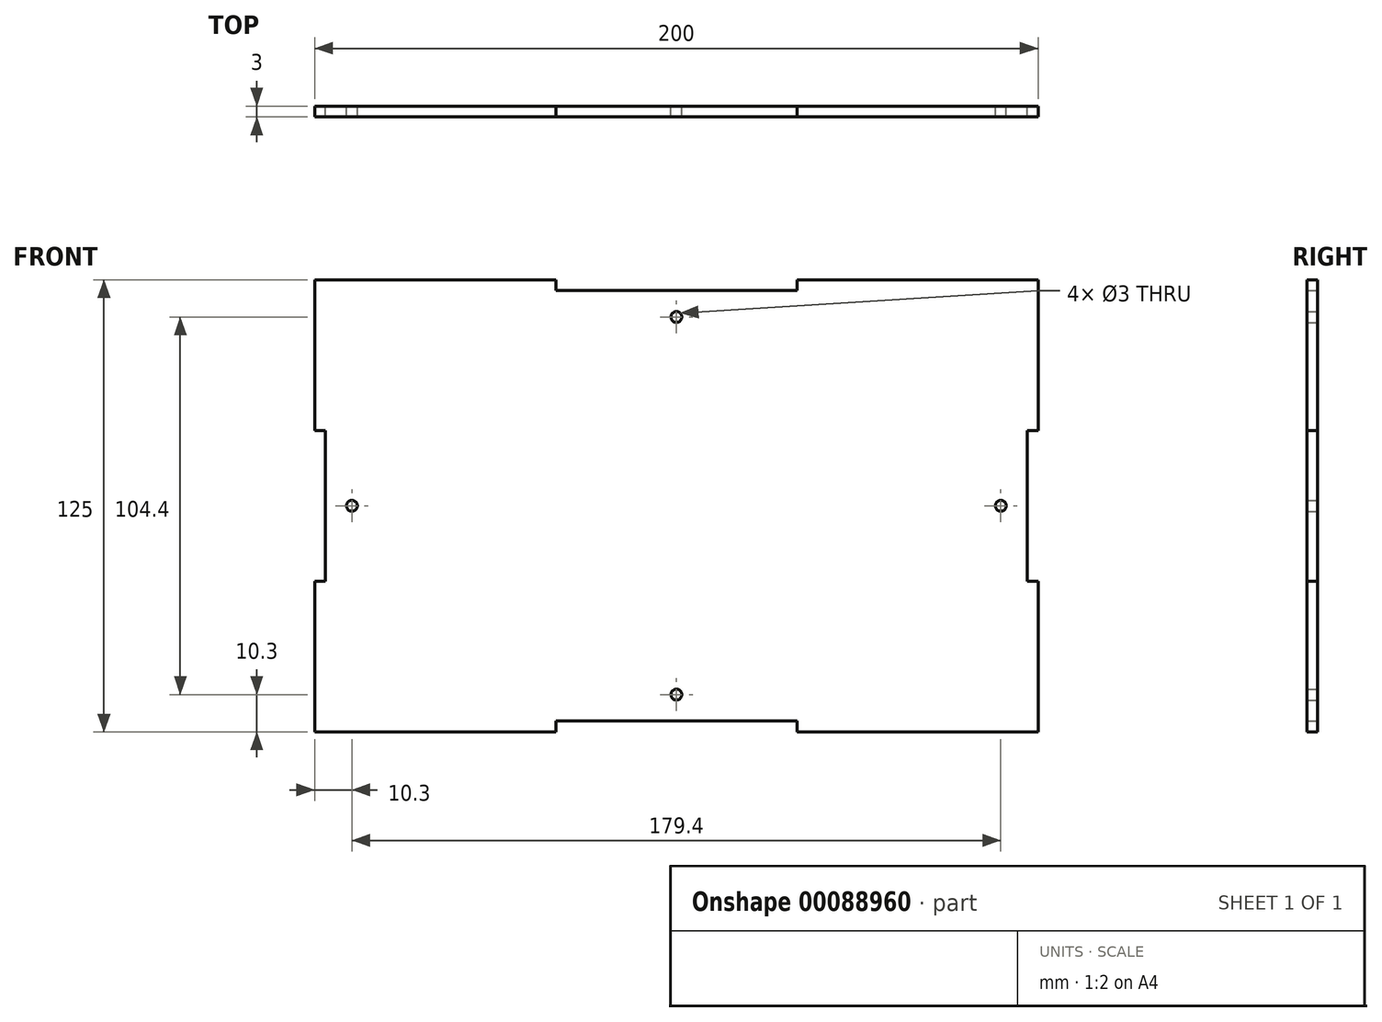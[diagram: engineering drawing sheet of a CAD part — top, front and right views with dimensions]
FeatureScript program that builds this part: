
annotation { "Feature Type Name" : "Feature", "Feature Type Description" : "" }
export const myFeature = defineFeature(function(context is Context, id is Id, definition is map)
    precondition{}
    {
        {
            var Q0;
            Q0=qCreatedBy(makeId("Front.planeOp"),FACE);
            var sketch = newSketch(context, id + "F0", { "sketchPlane" : qUnion([Q0])});
            skLineSegment(sketch, "E0.top", {"start": v(-100, -62.5) * mm, "end": v(-33.33, -62.5) * mm});
            skLineSegment(sketch, "E0.left", {"start": v(-100, 62.5) * mm, "end": v(-100, 20.83) * mm});
            skLineSegment(sketch, "E0.right", {"start": v(100, 62.5) * mm, "end": v(100, 20.83) * mm});
            skLineSegment(sketch, "E1", {"start": v(-100, 62.5) * mm, "end": v(-33.33, 62.5) * mm});
            skLineSegment(sketch, "E2", {"start": v(-33.33, 62.5) * mm, "end": v(-33.33, 59.5) * mm});
            skLineSegment(sketch, "E3", {"start": v(-33.33, 59.5) * mm, "end": v(33.33, 59.5) * mm});
            skLineSegment(sketch, "E4", {"start": v(33.33, 59.5) * mm, "end": v(33.33, 62.5) * mm});
            skLineSegment(sketch, "E5", {"start": v(33.33, 62.5) * mm, "end": v(100, 62.5) * mm});
            skLineSegment(sketch, "E6", {"start": v(100, 20.83) * mm, "end": v(97, 20.83) * mm});
            skLineSegment(sketch, "E7", {"start": v(97, 20.83) * mm, "end": v(97, -20.83) * mm});
            skLineSegment(sketch, "E8", {"start": v(97, -20.83) * mm, "end": v(100, -20.83) * mm});
            skLineSegment(sketch, "E9.trimOffspring", {"start": v(100, -20.83) * mm, "end": v(100, -62.5) * mm});
            skLineSegment(sketch, "E10", {"start": v(-100, 20.83) * mm, "end": v(-97, 20.83) * mm});
            skLineSegment(sketch, "E11", {"start": v(-97, 20.83) * mm, "end": v(-97, -20.83) * mm});
            skLineSegment(sketch, "E12", {"start": v(-97, -20.83) * mm, "end": v(-100, -20.83) * mm});
            skLineSegment(sketch, "E13", {"start": v(-33.33, -62.5) * mm, "end": v(-33.33, -59.5) * mm});
            skLineSegment(sketch, "E14", {"start": v(-33.33, -59.5) * mm, "end": v(33.33, -59.5) * mm});
            skLineSegment(sketch, "E15", {"start": v(33.33, -59.5) * mm, "end": v(33.33, -62.5) * mm});
            skLineSegment(sketch, "E16.trimOffspring", {"start": v(-100, -20.83) * mm, "end": v(-100, -62.5) * mm});
            skLineSegment(sketch, "E17.trimOffspring", {"start": v(33.33, -62.5) * mm, "end": v(100, -62.5) * mm});
            skCircle(sketch, "E18", {"center": v(0, 52.2) * mm, "radius": 1.5 * mm});
            skCircle(sketch, "E19", {"center": v(89.7, 0) * mm, "radius": 1.5 * mm});
            skCircle(sketch, "E20", {"center": v(0, -52.2) * mm, "radius": 1.5 * mm});
            skCircle(sketch, "E21", {"center": v(-89.7, 0) * mm, "radius": 1.5 * mm});
            skSolve(sketch);
        }
        {
            var Q0;
            Q0=qSketchRegion(id+"F0",true);
            extrude(context, id + "F1", {"entities" : qUnion([Q0]), "depth" : 3 * mm});
        }
        {
            var Q0;
            Q0=makeQuery(id+"F1.opExtrude","SWEPT_BODY",BODY,{"disambiguationData":[OSD([sQuery(id+"F0.wireOp",EDGE,"E0.top"),sQuery(id+"F0.wireOp",EDGE,"E0.left"),sQuery(id+"F0.wireOp",EDGE,"E0.right"),sQuery(id+"F0.wireOp",EDGE,"E1"),sQuery(id+"F0.wireOp",EDGE,"E2"),sQuery(id+"F0.wireOp",EDGE,"E3"),sQuery(id+"F0.wireOp",EDGE,"E4"),sQuery(id+"F0.wireOp",EDGE,"E5"),sQuery(id+"F0.wireOp",EDGE,"E6"),sQuery(id+"F0.wireOp",EDGE,"E7"),sQuery(id+"F0.wireOp",EDGE,"E8"),sQuery(id+"F0.wireOp",EDGE,"E9.trimOffspring"),sQuery(id+"F0.wireOp",EDGE,"E10"),sQuery(id+"F0.wireOp",EDGE,"E11"),sQuery(id+"F0.wireOp",EDGE,"E12"),sQuery(id+"F0.wireOp",EDGE,"E13"),sQuery(id+"F0.wireOp",EDGE,"E14"),sQuery(id+"F0.wireOp",EDGE,"E15"),sQuery(id+"F0.wireOp",EDGE,"E16.trimOffspring"),sQuery(id+"F0.wireOp",EDGE,"E17.trimOffspring"),sQuery(id+"F0.wireOp",EDGE,"iJvMOkkT-Gsvz-D80s-Lrck-NuYzV2775GFc"),sQuery(id+"F0.wireOp",EDGE,"95r7G61u-81NE-ogXZ-HZlh-HaEjHri7Uc5C"),sQuery(id+"F0.wireOp",EDGE,"kNa5tEdO-uy4Q-kRTS-gWff-R1CwjTJMmlwP"),sQuery(id+"F0.wireOp",EDGE,"NSmLs8Xq-7i2g-OZIT-hmmc-yelxhuIJ4KvX"),sQuery(id+"F0.wireOp",EDGE,"4YweHJoU-akzP-T6YO-Ozvt-s9SiKn9Ip7Ij"),sQuery(id+"F0.wireOp",EDGE,"DRZYSCKz-exI7-oD3f-2VZ2-mNw9MquuhidN"),sQuery(id+"F0.wireOp",EDGE,"cFZweqHX-i8zY-QQJQ-dr00-DEtuZUepJHJH"),sQuery(id+"F0.wireOp",EDGE,"vflKgIvX-I86b-ziDt-TOTA-sqA9vDxPemz3"),sQuery(id+"F0.wireOp",EDGE,"id5eZwnR-KPJp-Ahn8-yCwL-o96Leq0KhUuP"),sQuery(id+"F0.wireOp",EDGE,"E18"),sQuery(id+"F0.wireOp",EDGE,"E19"),sQuery(id+"F0.wireOp",EDGE,"E20"),sQuery(id+"F0.wireOp",EDGE,"E21")])]});
            transform(context, id + "F2", {"entities" : qUnion([Q0]), "transformType" : TransformType.TRANSLATION_3D, "dx" : 0 * mm, "dy" : 60 * mm, "dz" : 0 * mm, "makeCopy" : true});
        }
        {
            var Q0;
            Q0=makeQuery(id+"F2.opPattern","COPY",BODY,{"derivedFrom":makeQuery(id+"F1.opExtrude","SWEPT_BODY",BODY,{"disambiguationData":[OSD([sQuery(id+"F0.wireOp",EDGE,"E0.top"),sQuery(id+"F0.wireOp",EDGE,"E0.left"),sQuery(id+"F0.wireOp",EDGE,"E0.right"),sQuery(id+"F0.wireOp",EDGE,"E1"),sQuery(id+"F0.wireOp",EDGE,"E2"),sQuery(id+"F0.wireOp",EDGE,"E3"),sQuery(id+"F0.wireOp",EDGE,"E4"),sQuery(id+"F0.wireOp",EDGE,"E5"),sQuery(id+"F0.wireOp",EDGE,"E6"),sQuery(id+"F0.wireOp",EDGE,"E7"),sQuery(id+"F0.wireOp",EDGE,"E8"),sQuery(id+"F0.wireOp",EDGE,"E9.trimOffspring"),sQuery(id+"F0.wireOp",EDGE,"E10"),sQuery(id+"F0.wireOp",EDGE,"E11"),sQuery(id+"F0.wireOp",EDGE,"E12"),sQuery(id+"F0.wireOp",EDGE,"E13"),sQuery(id+"F0.wireOp",EDGE,"E14"),sQuery(id+"F0.wireOp",EDGE,"E15"),sQuery(id+"F0.wireOp",EDGE,"E16.trimOffspring"),sQuery(id+"F0.wireOp",EDGE,"E17.trimOffspring"),sQuery(id+"F0.wireOp",EDGE,"iJvMOkkT-Gsvz-D80s-Lrck-NuYzV2775GFc"),sQuery(id+"F0.wireOp",EDGE,"95r7G61u-81NE-ogXZ-HZlh-HaEjHri7Uc5C"),sQuery(id+"F0.wireOp",EDGE,"kNa5tEdO-uy4Q-kRTS-gWff-R1CwjTJMmlwP"),sQuery(id+"F0.wireOp",EDGE,"NSmLs8Xq-7i2g-OZIT-hmmc-yelxhuIJ4KvX"),sQuery(id+"F0.wireOp",EDGE,"4YweHJoU-akzP-T6YO-Ozvt-s9SiKn9Ip7Ij"),sQuery(id+"F0.wireOp",EDGE,"DRZYSCKz-exI7-oD3f-2VZ2-mNw9MquuhidN"),sQuery(id+"F0.wireOp",EDGE,"cFZweqHX-i8zY-QQJQ-dr00-DEtuZUepJHJH"),sQuery(id+"F0.wireOp",EDGE,"vflKgIvX-I86b-ziDt-TOTA-sqA9vDxPemz3"),sQuery(id+"F0.wireOp",EDGE,"id5eZwnR-KPJp-Ahn8-yCwL-o96Leq0KhUuP"),sQuery(id+"F0.wireOp",EDGE,"E18"),sQuery(id+"F0.wireOp",EDGE,"E19"),sQuery(id+"F0.wireOp",EDGE,"E20"),sQuery(id+"F0.wireOp",EDGE,"E21")])]}),"instanceName":"1"});
            deleteBodies(context, id + "F3", {"entities" : qUnion([Q0])});
        }
    });
